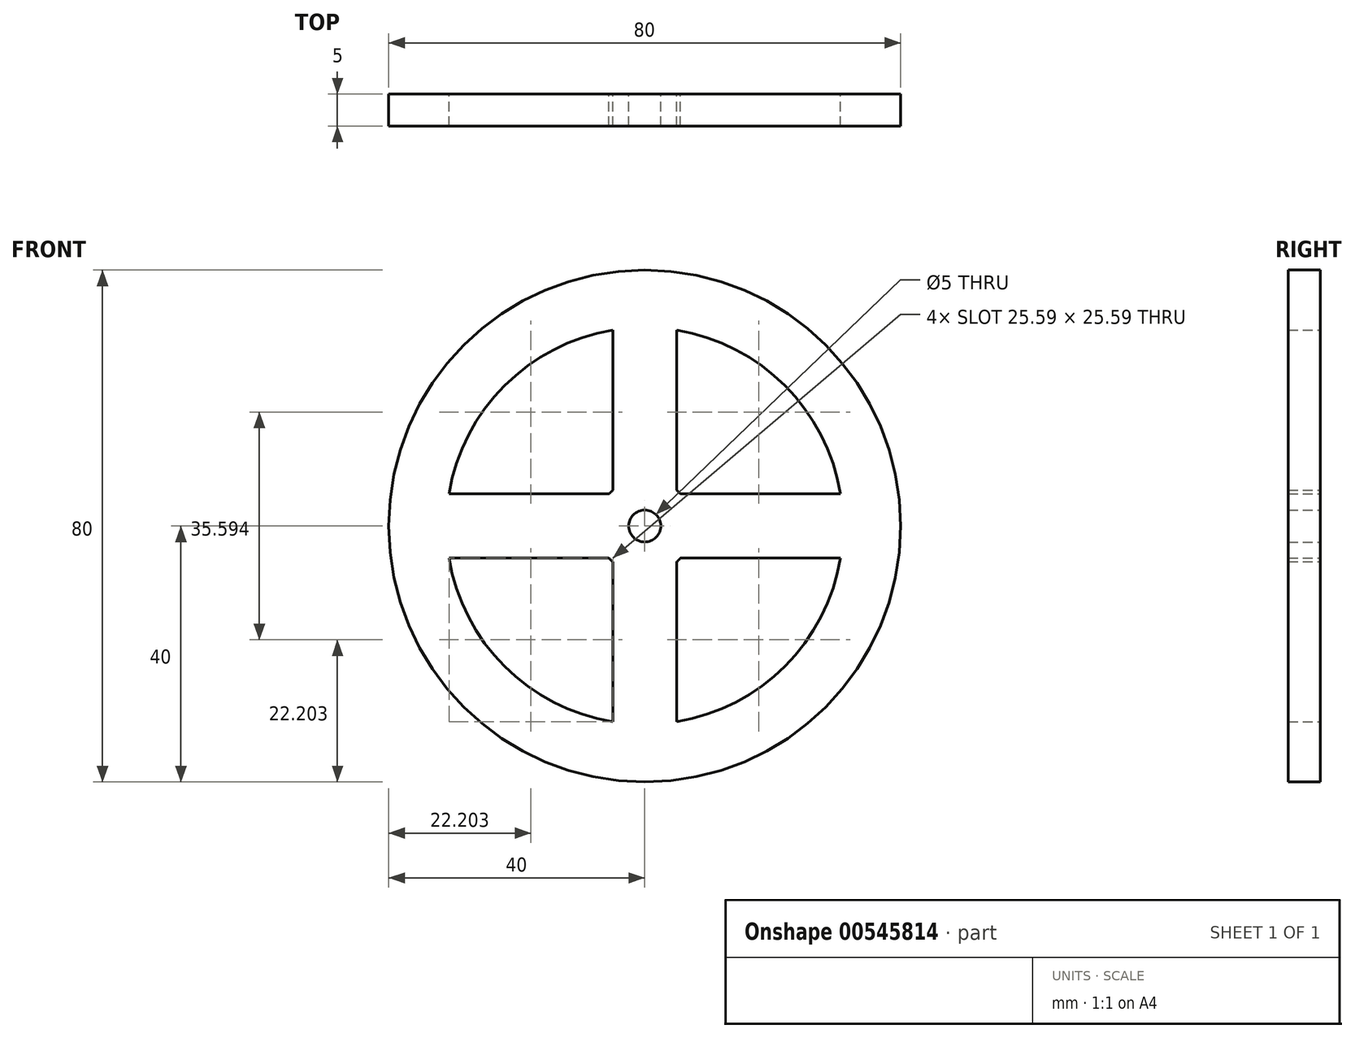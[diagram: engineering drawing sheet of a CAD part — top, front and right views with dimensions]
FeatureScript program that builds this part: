
annotation { "Feature Type Name" : "Feature", "Feature Type Description" : "" }
export const myFeature = defineFeature(function(context is Context, id is Id, definition is map)
    precondition{}
    {
        {
            var Q0;
            Q0=qCreatedBy(makeId("Front.planeOp"),FACE);
            var sketch = newSketch(context, id + "F0", { "sketchPlane" : qUnion([Q0])});
            skCircle(sketch, "E0", {"center": v(0, 0) * mm, "radius": 40 * mm});
            skArc(sketch, "E1", {"start": v(-30.6, -5) * mm, "mid": v(-21.92, -21.92) * mm, "end": v(-5, -30.6) * mm});
            skArc(sketch, "E2", {"start": v(5, -5.6) * mm, "mid": v(5.3, -5.3) * mm, "end": v(5.6, -5) * mm});
            skCircle(sketch, "E3", {"center": v(0, 0) * mm, "radius": 2.5 * mm});
            skLineSegment(sketch, "E4", {"start": v(0, 0) * mm, "end": v(0, 31) * mm, "construction": true});
            skLineSegment(sketch, "E5", {"start": v(0, 0) * mm, "end": v(-2.5, 0) * mm});
            skLineSegment(sketch, "E6", {"start": v(0, 0) * mm, "end": v(0, -31) * mm, "construction": true});
            skLineSegment(sketch, "E7", {"start": v(0, 0) * mm, "end": v(2.5, 0) * mm});
            skLineSegment(sketch, "E8.0", {"start": v(-5, 5.6) * mm, "end": v(-5, 30.6) * mm});
            skLineSegment(sketch, "E9.0", {"start": v(-5.6, 5) * mm, "end": v(-30.6, 5) * mm});
            skLineSegment(sketch, "E10.0", {"start": v(-5.6, -5) * mm, "end": v(-30.6, -5) * mm});
            skLineSegment(sketch, "E11.0", {"start": v(-5, -5.6) * mm, "end": v(-5, -30.6) * mm});
            skLineSegment(sketch, "E12.0", {"start": v(5, -5.6) * mm, "end": v(5, -30.6) * mm});
            skLineSegment(sketch, "E13.0", {"start": v(5.6, -5) * mm, "end": v(30.6, -5) * mm});
            skArc(sketch, "E14.trimOffspring", {"start": v(5, -30.6) * mm, "mid": v(21.92, -21.92) * mm, "end": v(30.6, -5) * mm});
            skArc(sketch, "E15.trimOffspring", {"start": v(30.6, 5) * mm, "mid": v(21.92, 21.92) * mm, "end": v(5, 30.6) * mm});
            skPoint(sketch, "E16.orphan", {"position": v(0, 40) * mm});
            skArc(sketch, "E17.trimOffspring", {"start": v(-5, 30.6) * mm, "mid": v(-21.92, 21.92) * mm, "end": v(-30.6, 5) * mm});
            skArc(sketch, "E18.trimOffspring", {"start": v(5.6, 5) * mm, "mid": v(5.3, 5.3) * mm, "end": v(5, 5.6) * mm});
            skArc(sketch, "E19.trimOffspring", {"start": v(-5.6, -5) * mm, "mid": v(-5.3, -5.3) * mm, "end": v(-5, -5.6) * mm});
            skLineSegment(sketch, "E20.trimOffspring", {"start": v(5.6, 5) * mm, "end": v(30.6, 5) * mm});
            skLineSegment(sketch, "E21.trimOffspring", {"start": v(5, 5.6) * mm, "end": v(5, 30.6) * mm});
            skArc(sketch, "E22.trimOffspring", {"start": v(-5, 5.6) * mm, "mid": v(-5.3, 5.3) * mm, "end": v(-5.6, 5) * mm});
            skLineSegment(sketch, "E23", {"start": v(0, 0) * mm, "end": v(2.5, 0) * mm, "construction": true});
            skSolve(sketch);
        }
        {
            var Q0;
            Q0=makeQuery(id+"F0.imprint","IMPRINT",FACE,{"disambiguationData":[TD([[makeQuery(id+"F0.imprint","IMPRINT",EDGE,{"derivedFrom":sQuery(id+"F0.wireOp",EDGE,"E0")}),1.0]])]});
            extrude(context, id + "F1", {"entities" : qUnion([Q0]), "endBound" : BoundingType.SYMMETRIC, "depth" : 5 * mm, "offsetDistance" : 25 * mm});
        }
    });
